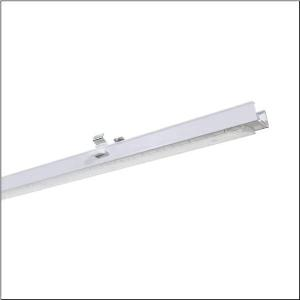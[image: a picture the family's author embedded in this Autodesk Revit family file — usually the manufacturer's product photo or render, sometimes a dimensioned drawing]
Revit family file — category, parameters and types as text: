
# Revit family: trunking_flex_31_51re18ma46b
name_source: partatom
category: Lighting Fixtures
units: mm (PartAtom-declared; Revit-internal decimal feet)

## family parameters
Cut with Voids When Loaded = No
Host = Face
Light Source = No
Part Type = Normal
Room Calculation Point = No
Round Connector Dimension = Use Diameter
Shared = No

## types (1)
- --- (1 x LED, 6400 lm, 40 W, 4000K)
    Apparent Load = 40 VA
    CIE Flux Codes = 71 89 97 97 100
    Color Rendering = 80
    Color Temperature = 4000K
    Default Elevation = 1800 mm
    Description = Trunking Flex 31, luminaire insert, of extruded aluminium section, coated, traffic white (RAL 9016), length: 1.172mm, width: 91mm, height: 53mm, LED rated luminous flux: 6.400lm, light colour: 840, control gear: ON/OFF Multilumen, with system connector: socket, mains connection: 220..240V, AC, 50/60Hz, rated input power: 40W, luminous flux adjustable on luminaire in four steps (3420/4540/5580/6630lm), connected load according to luminous flux setting (20/26/33/40W), primary light control with lens, of plastic, primary optical cover: cover, of PMMA, light emission: direct distribution, protection rating (complete): IP20, insulation class (complete): insulation class I (protective earthing), certification: CE, UKCA, impact resistance: IK02, permissible ambient temperature for indoor applications: -20..+40°C, packaging unit: 1 piece
    Height = 58 mm
    Lamp = 1 x LED
    Lamp Light Flux = 6400 lm
    Lamp Power = 40 W
    Lamp count = 1
    Length = 1172 mm
    Luminous efficacy = 160 lm/W
    Manufacturer = Siteco
    ModVariant = No
    Model = 51RE18MA46B
    Mounting Place = Ceiling
    Mounting Type = Pendant
    Number of Poles = 1
    OnlyDefault = Yes
    Power Factor = 1
    Product Name = Trunking Flex 31
    Product group = luminaire insert
    ProductGroupID = 901
    Protection Class = Protection class I
    Protection Degree = IP 20
    RLX_Detail_Level = 1
    RLX_Emergency_Light_Flux = 0 lm
    RLX_Emergency_Type = 0
    RLX_Emergency_Type_DB = No
    RlxData = <blob elided: 20061 chars, md5=817f3e53>
    Socket = socket
    Standby Power = 0 W
    System Light Flux = 6400 lm
    System Power = 40 W
    Type Comments = factory setting: luminous flux: 100 % | (ON | ON) | 300 mA
    Type Image = l_1266702.jpg
    URL = http://relux.com
    VarID = @adj_018601
    Voltage = 0 V
    Weight = 0.00 kg
    Width = 65 mm

## geometry (parser evidence)
native form markers: Blend x4, Sweep x10
no freeform markers — native parametric forms only
